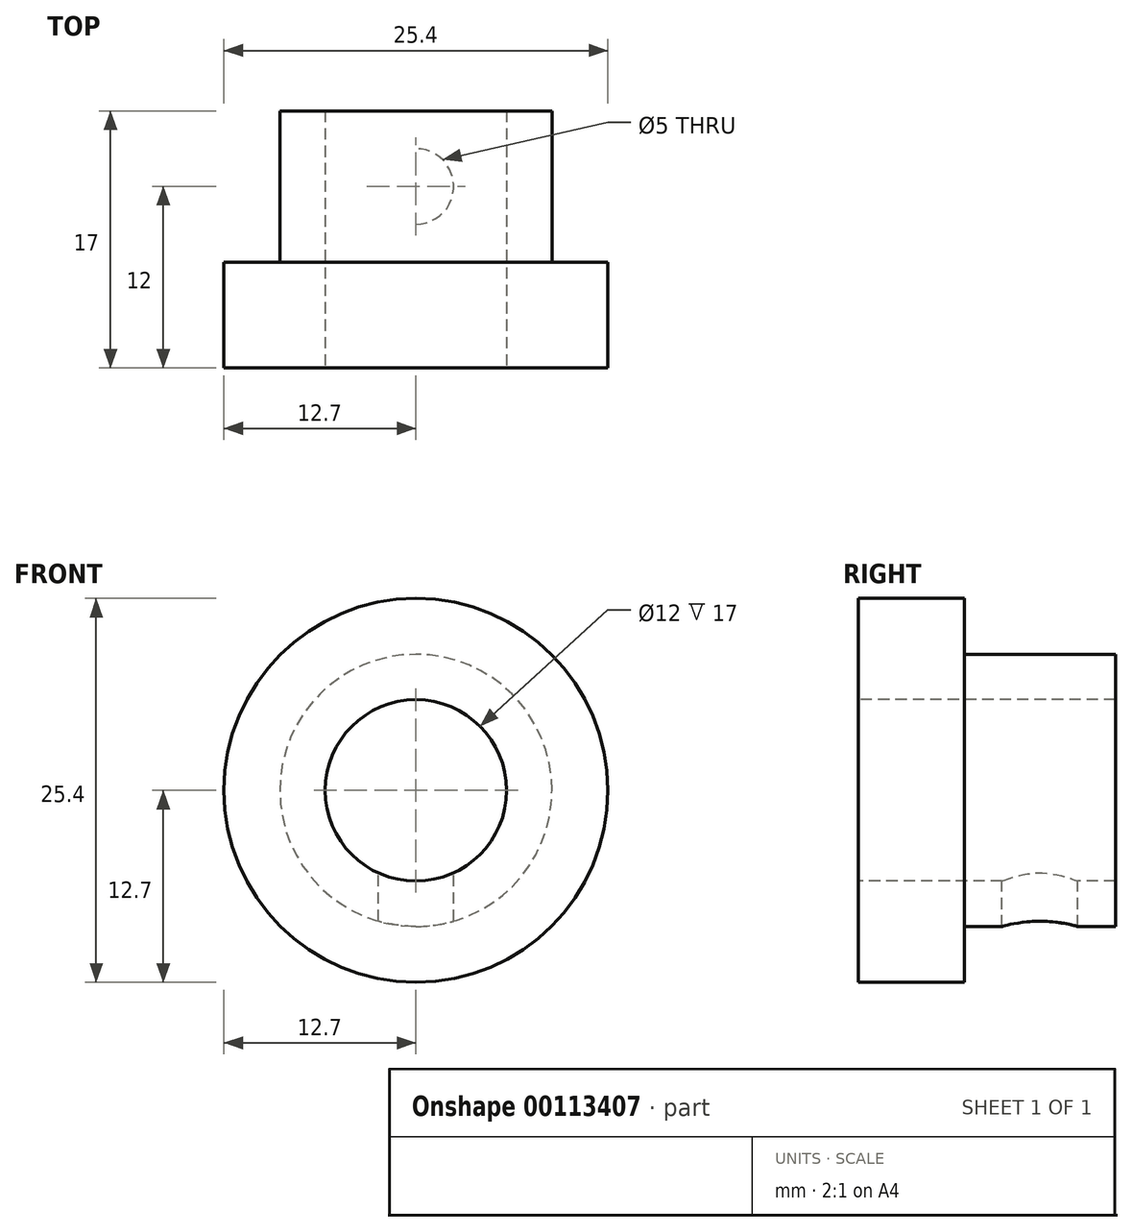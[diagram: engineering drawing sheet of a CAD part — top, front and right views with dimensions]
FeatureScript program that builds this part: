
annotation { "Feature Type Name" : "Feature", "Feature Type Description" : "" }
export const myFeature = defineFeature(function(context is Context, id is Id, definition is map)
    precondition{}
    {
        {
            var Q0;
            Q0=qCreatedBy(makeId("Front.planeOp"),FACE);
            var sketch = newSketch(context, id + "F0", { "sketchPlane" : qUnion([Q0])});
            skCircle(sketch, "E0", {"center": v(0, 0) * mm, "radius": 12.7 * mm});
            skSolve(sketch);
        }
        {
            var Q0;
            Q0=makeQuery(id+"F0.imprint","IMPRINT",FACE,{"disambiguationData":[TD([[makeQuery(id+"F0.imprint","IMPRINT",EDGE,{"derivedFrom":sQuery(id+"F0.wireOp",EDGE,"E0")}),1.0]])]});
            extrude(context, id + "F1", {"entities" : qUnion([Q0]), "depth" : 7 * mm});
        }
        {
            var Q0;
            Q0=qCreatedBy(makeId("Front.planeOp"),FACE);
            var sketch = newSketch(context, id + "F2", { "sketchPlane" : qUnion([Q0])});
            skCircle(sketch, "E1", {"center": v(0, 0) * mm, "radius": 9 * mm});
            skSolve(sketch);
        }
        {
            var Q0;
            Q0=makeQuery(id+"F2.imprint","IMPRINT",FACE,{"disambiguationData":[TD([[makeQuery(id+"F2.imprint","IMPRINT",EDGE,{"derivedFrom":sQuery(id+"F2.wireOp",EDGE,"E1")}),1.0]])]});
            extrude(context, id + "F3", {"entities" : qUnion([Q0]), "operationType" : NewBodyOperationType.ADD, "oppositeDirection" : true, "depth" : 10 * mm});
        }
        {
            var Q0;
            Q0=makeQuery(id+"F1.opExtrude","CAP_FACE",FACE,{"disambiguationData":[OSD([sQuery(id+"F0.wireOp",EDGE,"E0")])],"isStart":false});
            var sketch = newSketch(context, id + "F4", { "sketchPlane" : qUnion([Q0])});
            skCircle(sketch, "E2", {"center": v(0, 0) * mm, "radius": 6 * mm});
            skSolve(sketch);
        }
        {
            var Q0;
            Q0=makeQuery(id+"F4.imprint","IMPRINT",FACE,{"disambiguationData":[TD([[makeQuery(id+"F4.imprint","IMPRINT",EDGE,{"derivedFrom":sQuery(id+"F4.wireOp",EDGE,"E2")}),1.0]])]});
            var Q1;
            Q1=sQuery(id+"F4.wireOp",EDGE,"E2");
            extrude(context, id + "F5", {"entities" : qUnion([Q0]), "operationType" : NewBodyOperationType.REMOVE, "surfaceEntities" : qUnion([Q1]), "endBound" : BoundingType.THROUGH_ALL, "oppositeDirection" : true, "depth" : 25 * mm});
        }
        {
            var Q0;
            Q0=qCreatedBy(makeId("Top.planeOp"),FACE);
            var sketch = newSketch(context, id + "F6", { "sketchPlane" : qUnion([Q0])});
            skPoint(sketch, "E3", {"position": v(0, 5) * mm});
            skSolve(sketch);
        }
        {
            var Q0;
            Q0=sQuery(id+"F6.wireOp",VERTEX,"E3");
            var Q1;
            Q1=makeQuery(id+"F1.opExtrude","SWEPT_BODY",BODY,{"disambiguationData":[OSD([sQuery(id+"F0.wireOp",EDGE,"E0")])]});
            hole(context, id + "F7", {"style" : HoleStyle.SIMPLE, "endStyle" : HoleEndStyle.THROUGH, "holeDiameter" : 5 * mm, "locations" : qUnion([Q0]), "scope" : qUnion([Q1]), "isTappedThrough" : true});
        }
    });
